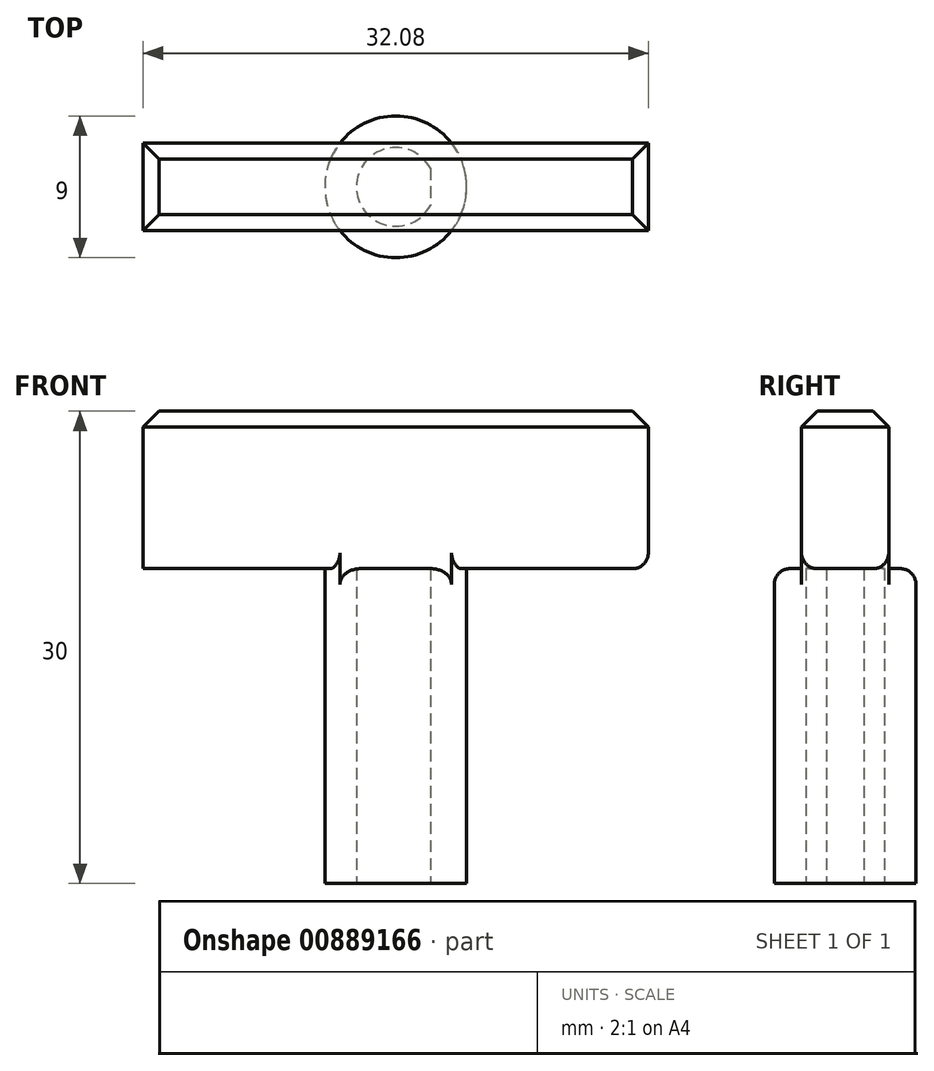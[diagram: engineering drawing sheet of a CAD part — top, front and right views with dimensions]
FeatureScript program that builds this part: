
annotation { "Feature Type Name" : "Feature", "Feature Type Description" : "" }
export const myFeature = defineFeature(function(context is Context, id is Id, definition is map)
    precondition{}
    {
        {
            var Q0;
            Q0=qCreatedBy(makeId("Top.planeOp"),FACE);
            var sketch = newSketch(context, id + "F0", { "sketchPlane" : qUnion([Q0])});
            skCircle(sketch, "E0", {"center": v(0, 0) * mm, "radius": 2.5 * mm});
            skCircle(sketch, "E1.0", {"center": v(0, 0) * mm, "radius": 4.5 * mm});
            skLineSegment(sketch, "E2", {"start": v(2.2, 1.19) * mm, "end": v(2.2, -1.19) * mm});
            skSolve(sketch);
        }
        {
            var Q0;
            Q0 = qSketchRegion(id + "F0", true);
            var Q1;
            Q1=makeQuery(id+"F0.imprint","IMPRINT",FACE,{"disambiguationData":[TD([[makeQuery(id+"F0.imprint","IMPRINT",EDGE,{"derivedFrom":sQuery(id+"F0.wireOp",EDGE,"E1.0")}),1.0]])]});
            var Q2;
            {var subQ0=sQuery(id+"F0.wireOp",EDGE,"E2");Q2=makeQuery(id+"F0.imprint","IMPRINT",FACE,{"disambiguationData":[TD([[makeQuery(id+"F0.imprint","IMPRINT",EDGE,{"derivedFrom":subQ0}),1.0]])]});}
            extrude(context, id + "F1", {"entities" : qUnion([Q0, Q1, Q2]), "depth" : 20 * mm, "offsetDistance" : 25 * mm});
        }
        {
            var Q0;
            Q0=makeQuery(id+"F1.opExtrude","CAP_FACE",FACE,{"disambiguationData":[OSD([sQuery(id+"F0.wireOp",EDGE,"E0"),sQuery(id+"F0.wireOp",EDGE,"E1.0"),sQuery(id+"F0.wireOp",EDGE,"E2")])],"isStart":false});
            var sketch = newSketch(context, id + "F2", { "sketchPlane" : qUnion([Q0])});
            skLineSegment(sketch, "E3.bottom", {"start": v(-3.54, 2.77) * mm, "end": v(3.54, 2.77) * mm});
            skLineSegment(sketch, "E3.top", {"start": v(-3.54, -2.77) * mm, "end": v(3.54, -2.77) * mm});
            skLineSegment(sketch, "E3.left", {"start": v(-3.54, 2.77) * mm, "end": v(-3.54, -2.77) * mm});
            skLineSegment(sketch, "E3.right", {"start": v(3.54, 2.77) * mm, "end": v(3.54, -2.77) * mm});
            skSolve(sketch);
        }
        {
            var Q0;
            Q0=makeQuery(id+"F2.imprint","IMPRINT",FACE,{"disambiguationData":[TD([[makeQuery(id+"F2.imprint","IMPRINT",EDGE,{"derivedFrom":makeQuery(id+"F1.opExtrude","CAP_EDGE",EDGE,{"disambiguationData":[OSD([sQuery(id+"F0.wireOp",EDGE,"E0")])],"isStart":false})}),1.0]])]});
            var Q1;
            Q1=makeQuery(id+"F2.imprint","IMPRINT",FACE,{"disambiguationData":[TD([[makeQuery(id+"F2.imprint","IMPRINT",EDGE,{"derivedFrom":sQuery(id+"F2.wireOp",EDGE,"E3.bottom")}),-1.0]])]});
            extrude(context, id + "F3", {"entities" : qUnion([Q0, Q1]), "operationType" : NewBodyOperationType.ADD, "depth" : 10 * mm, "offsetDistance" : 25 * mm});
        }
        {
            var Q0;
            Q0=makeQuery(id+"F3.opExtrude","SWEPT_FACE",FACE,{"disambiguationData":[OSD([sQuery(id+"F2.wireOp",EDGE,"E3.right")])]});
            var Q1;
            Q1=makeQuery(id+"F3.opExtrude","SWEPT_FACE",FACE,{"disambiguationData":[OSD([sQuery(id+"F2.wireOp",EDGE,"E3.left")])]});
            extrude(context, id + "F4", {"entities" : qUnion([Q0, Q1]), "operationType" : NewBodyOperationType.ADD, "endBound" : BoundingType.SYMMETRIC, "depth" : 25 * mm, "offsetDistance" : 25 * mm});
        }
        {
            var Q0;
            {var subQ0=sQuery(id+"F2.wireOp",EDGE,"E3.right");var subQ1=sQuery(id+"F2.wireOp",EDGE,"E3.top");var subQ2=sQuery(id+"F0.wireOp",EDGE,"E1.0");var subQ3=sQuery(id+"F2.wireOp",EDGE,"E3.left");Q0=makeQuery(id+"F4.boolean.opBoolean","MERGE",EDGE,{"derivedFrom":[makeQuery(id+"F3.opExtrude","CAP_EDGE",EDGE,{"disambiguationData":[OSD([subQ1])],"isStart":false}),makeQuery(id+"F4.opExtrude","SWEPT_EDGE",EDGE,{"disambiguationData":[OSD([subQ2,subQ1,subQ3]),TDD([makeQuery(id+"F3.opExtrude","CAP_VERTEX",VERTEX,{"disambiguationData":[OSD([subQ2,subQ1,subQ3])],"isStart":false})])]}),makeQuery(id+"F4.opExtrude","SWEPT_EDGE",EDGE,{"disambiguationData":[OSD([subQ2,subQ1,subQ0]),TDD([makeQuery(id+"F3.opExtrude","CAP_VERTEX",VERTEX,{"disambiguationData":[OSD([subQ2,subQ1,subQ0])],"isStart":false})])]})]});}
            var Q1;
            {var subQ0=sQuery(id+"F2.wireOp",EDGE,"E3.right");var subQ1=sQuery(id+"F2.wireOp",EDGE,"E3.bottom");var subQ2=sQuery(id+"F0.wireOp",EDGE,"E1.0");var subQ3=sQuery(id+"F2.wireOp",EDGE,"E3.left");Q1=makeQuery(id+"F4.boolean.opBoolean","MERGE",EDGE,{"derivedFrom":[makeQuery(id+"F3.opExtrude","CAP_EDGE",EDGE,{"disambiguationData":[OSD([subQ1])],"isStart":false}),makeQuery(id+"F4.opExtrude","SWEPT_EDGE",EDGE,{"disambiguationData":[OSD([subQ2,subQ1,subQ3]),TDD([makeQuery(id+"F3.opExtrude","CAP_VERTEX",VERTEX,{"disambiguationData":[OSD([subQ2,subQ1,subQ3])],"isStart":false})])]}),makeQuery(id+"F4.opExtrude","SWEPT_EDGE",EDGE,{"disambiguationData":[OSD([subQ2,subQ1,subQ0]),TDD([makeQuery(id+"F3.opExtrude","CAP_VERTEX",VERTEX,{"disambiguationData":[OSD([subQ2,subQ1,subQ0])],"isStart":false})])]})]});}
            var Q2;
            {var subQ0=sQuery(id+"F2.wireOp",EDGE,"E3.right");Q2=makeQuery(id+"F4.opExtrude","CAP_EDGE",EDGE,{"disambiguationData":[OSD([subQ0]),TDD([makeQuery(id+"F3.opExtrude","CAP_EDGE",EDGE,{"disambiguationData":[OSD([subQ0])],"isStart":false})])],"isStart":false});}
            var Q3;
            {var subQ0=sQuery(id+"F2.wireOp",EDGE,"E3.left");Q3=makeQuery(id+"F4.opExtrude","CAP_EDGE",EDGE,{"disambiguationData":[OSD([subQ0]),TDD([makeQuery(id+"F3.opExtrude","CAP_EDGE",EDGE,{"disambiguationData":[OSD([subQ0])],"isStart":false})])],"isStart":true});}
            chamfer(context, id + "F5", {"entities" : qUnion([Q0, Q1, Q2, Q3]), "width" : 1 * mm, "tangentPropagation" : true});
        }
        {
            var Q0;
            {var subQ0=sQuery(id+"F0.wireOp",EDGE,"E1.0");Q0=makeQuery(id+"F3.boolean.opBoolean","SPLIT",EDGE,{"disambiguationData":[TD([makeQuery(id+"F1.opExtrude","CAP_FACE",FACE,{"disambiguationData":[OSD([sQuery(id+"F0.wireOp",EDGE,"E0"),subQ0,sQuery(id+"F0.wireOp",EDGE,"E2")])],"isStart":false}),makeQuery(id+"F1.opExtrude","SWEPT_FACE",FACE,{"disambiguationData":[OSD([subQ0])]}),makeQuery(id+"F3.opExtrude","SWEPT_FACE",FACE,{"disambiguationData":[OSD([sQuery(id+"F2.wireOp",EDGE,"E3.bottom")])]}),makeQuery(id+"F3.opExtrude","SWEPT_FACE",FACE,{"disambiguationData":[OSD([sQuery(id+"F2.wireOp",EDGE,"E3.left")])]}),makeQuery(id+"F3.opExtrude","SWEPT_FACE",FACE,{"disambiguationData":[OSD([sQuery(id+"F2.wireOp",EDGE,"E3.right")])]})])],"derivedFrom":makeQuery(id+"F1.opExtrude","CAP_EDGE",EDGE,{"disambiguationData":[OSD([subQ0])],"isStart":false})});}
            var Q1;
            {var subQ0=sQuery(id+"F0.wireOp",EDGE,"E1.0");Q1=makeQuery(id+"F3.boolean.opBoolean","SPLIT",EDGE,{"disambiguationData":[TD([makeQuery(id+"F1.opExtrude","CAP_FACE",FACE,{"disambiguationData":[OSD([sQuery(id+"F0.wireOp",EDGE,"E0"),subQ0,sQuery(id+"F0.wireOp",EDGE,"E2")])],"isStart":false}),makeQuery(id+"F1.opExtrude","SWEPT_FACE",FACE,{"disambiguationData":[OSD([subQ0])]}),makeQuery(id+"F3.opExtrude","SWEPT_FACE",FACE,{"disambiguationData":[OSD([sQuery(id+"F2.wireOp",EDGE,"E3.top")])]}),makeQuery(id+"F3.opExtrude","SWEPT_FACE",FACE,{"disambiguationData":[OSD([sQuery(id+"F2.wireOp",EDGE,"E3.left")])]}),makeQuery(id+"F3.opExtrude","SWEPT_FACE",FACE,{"disambiguationData":[OSD([sQuery(id+"F2.wireOp",EDGE,"E3.right")])]})])],"derivedFrom":makeQuery(id+"F1.opExtrude","CAP_EDGE",EDGE,{"disambiguationData":[OSD([subQ0])],"isStart":false})});}
            fillet(context, id + "F6", {"entities" : qUnion([Q0, Q1]), "radius" : 1 * mm, "tangentPropagation" : true, "allowEdgeOverflow" : false});
        }
        {
            var Q0;
            {var subQ0=sQuery(id+"F2.wireOp",EDGE,"E3.right");var subQ1=sQuery(id+"F2.wireOp",EDGE,"E3.bottom");var subQ2=sQuery(id+"F0.wireOp",EDGE,"E1.0");var subQ3=sQuery(id+"F2.wireOp",EDGE,"E3.left");Q0=makeQuery(id+"F4.boolean.opBoolean","MERGE",EDGE,{"disambiguationData":[OD(1.0)],"derivedFrom":[makeQuery(id+"F4.opExtrude","SWEPT_EDGE",EDGE,{"disambiguationData":[OSD([subQ2,subQ1,subQ3]),TDD([makeQuery(id+"F3.opExtrude","CAP_VERTEX",VERTEX,{"disambiguationData":[OSD([subQ2,subQ1,subQ3])],"isStart":true})])]}),makeQuery(id+"F4.opExtrude","SWEPT_EDGE",EDGE,{"disambiguationData":[OSD([subQ2,subQ1,subQ0]),TDD([makeQuery(id+"F3.opExtrude","CAP_VERTEX",VERTEX,{"disambiguationData":[OSD([subQ2,subQ1,subQ0])],"isStart":true})])]})]});}
            var Q1;
            {var subQ0=sQuery(id+"F2.wireOp",EDGE,"E3.right");var subQ1=sQuery(id+"F2.wireOp",EDGE,"E3.top");var subQ2=sQuery(id+"F0.wireOp",EDGE,"E1.0");var subQ3=sQuery(id+"F2.wireOp",EDGE,"E3.left");Q1=makeQuery(id+"F4.boolean.opBoolean","MERGE",EDGE,{"disambiguationData":[OD(1.0)],"derivedFrom":[makeQuery(id+"F4.opExtrude","SWEPT_EDGE",EDGE,{"disambiguationData":[OSD([subQ2,subQ1,subQ3]),TDD([makeQuery(id+"F3.opExtrude","CAP_VERTEX",VERTEX,{"disambiguationData":[OSD([subQ2,subQ1,subQ3])],"isStart":true})])]}),makeQuery(id+"F4.opExtrude","SWEPT_EDGE",EDGE,{"disambiguationData":[OSD([subQ2,subQ1,subQ0]),TDD([makeQuery(id+"F3.opExtrude","CAP_VERTEX",VERTEX,{"disambiguationData":[OSD([subQ2,subQ1,subQ0])],"isStart":true})])]})]});}
            var Q2;
            {var subQ0=sQuery(id+"F2.wireOp",EDGE,"E3.right");Q2=makeQuery(id+"F4.opExtrude","CAP_EDGE",EDGE,{"disambiguationData":[OSD([subQ0]),TDD([makeQuery(id+"F3.opExtrude","CAP_EDGE",EDGE,{"disambiguationData":[OSD([subQ0])],"isStart":true})])],"isStart":false});}
            var Q3;
            {var subQ0=sQuery(id+"F2.wireOp",EDGE,"E3.right");var subQ1=sQuery(id+"F2.wireOp",EDGE,"E3.top");var subQ2=sQuery(id+"F0.wireOp",EDGE,"E1.0");var subQ3=sQuery(id+"F2.wireOp",EDGE,"E3.left");Q3=makeQuery(id+"F4.boolean.opBoolean","MERGE",EDGE,{"disambiguationData":[OD(0.0)],"derivedFrom":[makeQuery(id+"F4.opExtrude","SWEPT_EDGE",EDGE,{"disambiguationData":[OSD([subQ2,subQ1,subQ3]),TDD([makeQuery(id+"F3.opExtrude","CAP_VERTEX",VERTEX,{"disambiguationData":[OSD([subQ2,subQ1,subQ3])],"isStart":true})])]}),makeQuery(id+"F4.opExtrude","SWEPT_EDGE",EDGE,{"disambiguationData":[OSD([subQ2,subQ1,subQ0]),TDD([makeQuery(id+"F3.opExtrude","CAP_VERTEX",VERTEX,{"disambiguationData":[OSD([subQ2,subQ1,subQ0])],"isStart":true})])]})]});}
            var Q4;
            {var subQ0=sQuery(id+"F2.wireOp",EDGE,"E3.right");var subQ1=sQuery(id+"F2.wireOp",EDGE,"E3.bottom");var subQ2=sQuery(id+"F0.wireOp",EDGE,"E1.0");var subQ3=sQuery(id+"F2.wireOp",EDGE,"E3.left");Q4=makeQuery(id+"F4.boolean.opBoolean","MERGE",EDGE,{"disambiguationData":[OD(0.0)],"derivedFrom":[makeQuery(id+"F4.opExtrude","SWEPT_EDGE",EDGE,{"disambiguationData":[OSD([subQ2,subQ1,subQ3]),TDD([makeQuery(id+"F3.opExtrude","CAP_VERTEX",VERTEX,{"disambiguationData":[OSD([subQ2,subQ1,subQ3])],"isStart":true})])]}),makeQuery(id+"F4.opExtrude","SWEPT_EDGE",EDGE,{"disambiguationData":[OSD([subQ2,subQ1,subQ0]),TDD([makeQuery(id+"F3.opExtrude","CAP_VERTEX",VERTEX,{"disambiguationData":[OSD([subQ2,subQ1,subQ0])],"isStart":true})])]})]});}
            var Q5;
            {var subQ0=sQuery(id+"F2.wireOp",EDGE,"E3.left");Q5=makeQuery(id+"F4.opExtrude","CAP_EDGE",EDGE,{"disambiguationData":[OSD([subQ0]),TDD([makeQuery(id+"F3.opExtrude","CAP_EDGE",EDGE,{"disambiguationData":[OSD([subQ0])],"isStart":true})])],"isStart":true});}
            fillet(context, id + "F7", {"entities" : qUnion([Q0, Q1, Q2, Q3, Q4, Q5]), "radius" : 1 * mm, "tangentPropagation" : true, "allowEdgeOverflow" : false});
        }
    });
